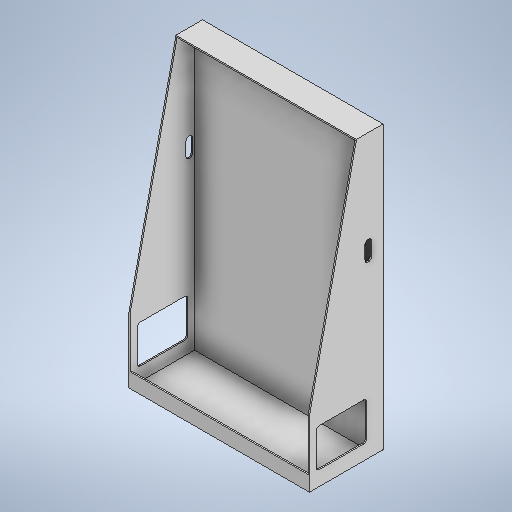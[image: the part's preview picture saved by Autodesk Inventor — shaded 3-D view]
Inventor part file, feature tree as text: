
AUTODESK INVENTOR PART (.ipt)
format: ipt  version: 2025 (Build 290162010, 162A)  size: 317,952 bytes
history: native  units: mm
features: extrude x4, sketch x4
ambient origin geometry x8: Origin, YZ Plane, XZ Plane, XY Plane, X Axis, Y Axis, Z Axis, Center Point
bodies: Solid1 (feature_tree)
feature tree (8):
  extrude  "Extrusion1"  Depth=2110.0mm
  extrude  "Extrusion2"  Depth=200.0mm
  extrude  "Extrusion3"  Depth=380.0mm
  extrude  "Extrusion4"  Depth=110.0mm
  sketch  "Sketch1"  dims[d0=550.0mm d1=2110.0mm]
  sketch  "Sketch2"  dims[d2=495.0mm d3=200.0mm]
  sketch  "Sketch3"  dims[d4=10.0mm d5=380.0mm]
  sketch  "Sketch4"  dims[d6=285.0mm d10=110.0mm d11=120.0mm d12=25.0mm d13=50.0mm d14=150.0mm d15=1270.0mm d16=85.0mm d17=25.0mm d18=1350.0mm d19=0.0mm d20=10.0mm d21=10.0mm d22=10.0mm d23=0.0mm d24=60.0mm d25=0.0mm d26=10.0mm d27=10.0mm d28=10.0mm d29=110.0mm d30=480.0mm d31=0.0mm d32=10.0mm d33=10.0mm d34=10.0mm d35=10.0mm d36=100.0mm d37=0.0mm]
